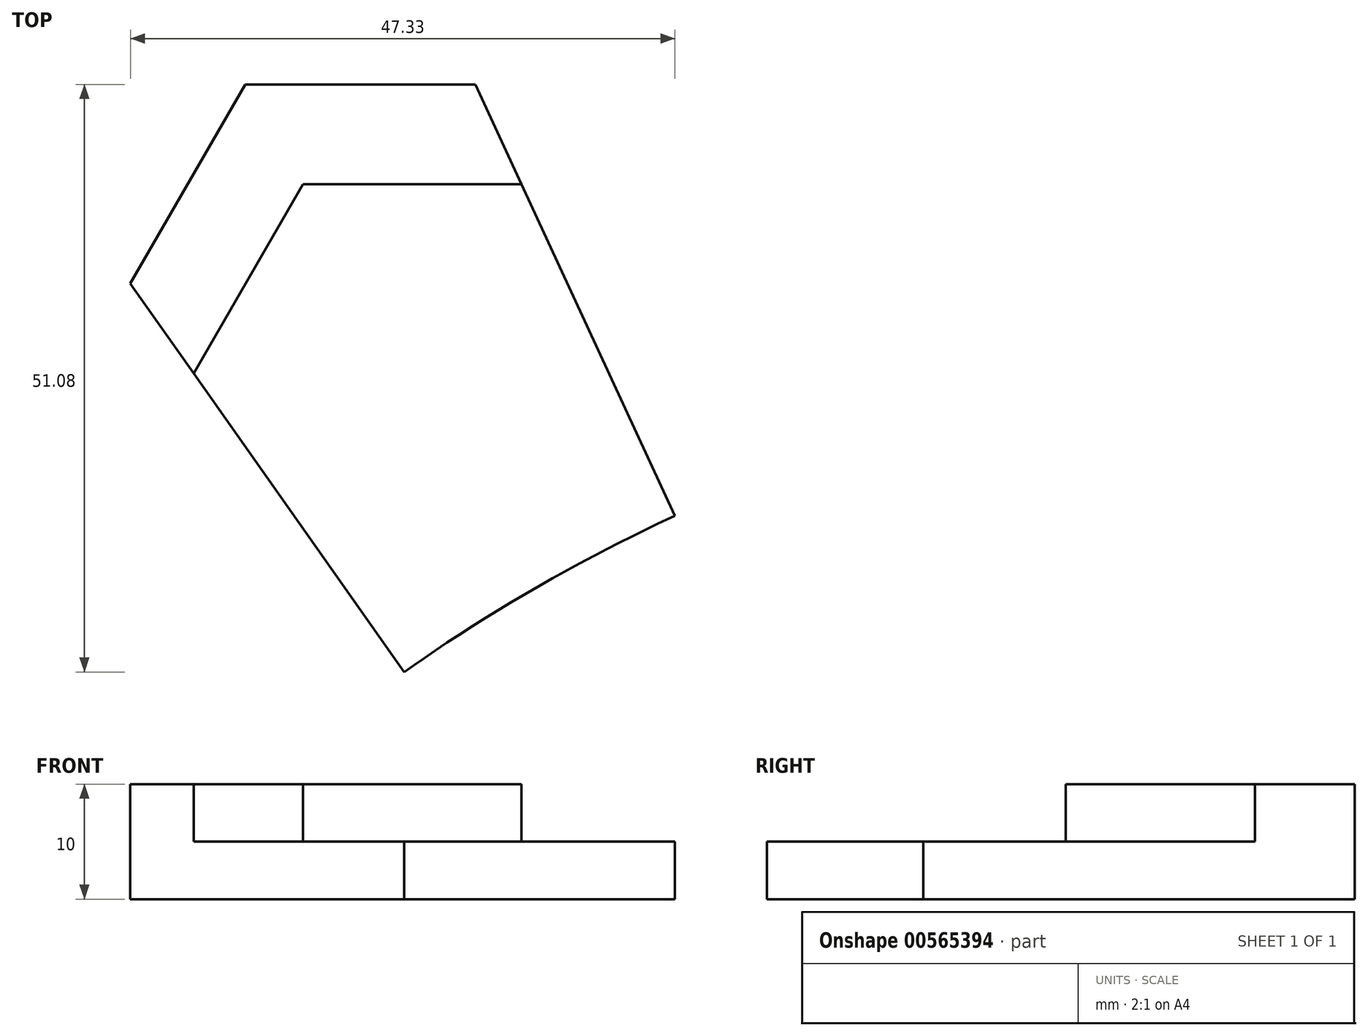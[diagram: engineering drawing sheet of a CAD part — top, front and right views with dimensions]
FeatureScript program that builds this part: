
annotation { "Feature Type Name" : "Feature", "Feature Type Description" : "" }
export const myFeature = defineFeature(function(context is Context, id is Id, definition is map)
    precondition{}
    {
        {
            var Q0;
            Q0=qCreatedBy(makeId("Top.planeOp"),FACE);
            var sketch = newSketch(context, id + "F0", { "sketchPlane" : qUnion([Q0])});
            skLineSegment(sketch, "E0", {"start": v(-110.26, 156.34) * mm, "end": v(-100.26, 173.66) * mm});
            skLineSegment(sketch, "E1", {"start": v(-100.26, 173.66) * mm, "end": v(-80.26, 173.66) * mm});
            skLineSegment(sketch, "E2", {"start": v(-110.26, 156.34) * mm, "end": v(-86.45, 122.58) * mm});
            skLineSegment(sketch, "E3", {"start": v(-80.26, 173.66) * mm, "end": v(-62.93, 136.16) * mm});
            skLineSegment(sketch, "E4", {"start": v(-100.26, 173.66) * mm, "end": v(-95.26, 165) * mm});
            skFitSpline(sketch, "E5", {"points": [v(-86.45, 122.58) * mm, v(-84.11, 124.2) * mm, v(-80.7, 126.44) * mm, v(-76.94, 128.76) * mm, v(-73.04, 131.01) * mm, v(-70.6, 132.34) * mm, v(-68.02, 133.7) * mm, v(-64.55, 135.4) * mm, v(-62.93, 136.16) * mm], "startDerivative": vector(19.68, 12.86) * mm, "endDerivative": vector(15.53, 7.74) * mm});
            skLineSegment(sketch, "E6", {"start": v(-104.76, 148.54) * mm, "end": v(-95.26, 165) * mm});
            skLineSegment(sketch, "E7", {"start": v(-76.26, 165) * mm, "end": v(-95.26, 165) * mm});
            skSolve(sketch);
        }
        {
            var Q0;
            {var subQ0=sQuery(id+"F0.wireOp",EDGE,"E5");Q0=makeQuery(id+"F0.imprint","IMPRINT",FACE,{"disambiguationData":[TD([[makeQuery(id+"F0.imprint","IMPRINT",EDGE,{"derivedFrom":subQ0}),1.0]])]});}
            extrude(context, id + "F1", {"entities" : qUnion([Q0]), "depth" : 5 * mm, "offsetDistance" : 25 * mm});
        }
        {
            var Q0;
            {var subQ0=sQuery(id+"F0.wireOp",EDGE,"E1");Q0=makeQuery(id+"F0.imprint","IMPRINT",FACE,{"disambiguationData":[TD([[makeQuery(id+"F0.imprint","IMPRINT",EDGE,{"derivedFrom":subQ0}),-1.0]])]});}
            var Q1;
            {var subQ0=sQuery(id+"F0.wireOp",EDGE,"E0");Q1=makeQuery(id+"F0.imprint","IMPRINT",FACE,{"disambiguationData":[TD([[makeQuery(id+"F0.imprint","IMPRINT",EDGE,{"derivedFrom":subQ0}),-1.0]])]});}
            extrude(context, id + "F2", {"entities" : qUnion([Q0, Q1]), "operationType" : NewBodyOperationType.ADD, "depth" : 10 * mm, "offsetDistance" : 25 * mm});
        }
    });
